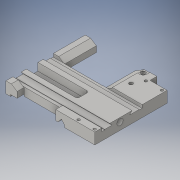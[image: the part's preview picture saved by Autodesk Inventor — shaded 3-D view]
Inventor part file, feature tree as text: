
AUTODESK INVENTOR PART (.ipt)
format: ipt  version: 2016 (Build 200138000, 138)  size: 288,768 bytes
history: native  units: in
note: dims shown in document units (in); Inventor stores cm internally (conversion verified against a paired STEP export)
features: extrude x18, sketch x18
ambient origin geometry x8: Origin, YZ Plane, XZ Plane, XY Plane, X Axis, Y Axis, Z Axis, Center Point
bodies: Solid1 (feature_tree)
feature tree (36):
  extrude  "Extrusion1"  Depth=13.5039in
  extrude  "Extrusion2"  Depth=1.9094in TaperAngle=0.0deg
  extrude  "Extrusion3"  Depth=1.378in
  extrude  "Extrusion4"  Depth=0.8933in
  extrude  "Extrusion5"  Depth=0.0787in
  extrude  "Extrusion6"  Depth=1.1811in
  extrude  "Extrusion7"  Depth=0.1181in
  extrude  "Extrusion8"  Depth=0.3937in
  extrude  "Extrusion10"  Depth=6.5748in
  extrude  "Extrusion11"  Depth=1.9094in TaperAngle=0.0deg
  extrude  "Extrusion12"  Depth=1.9094in TaperAngle=0.0deg
  extrude  "Extrusion16"  Depth=1.2992in TaperAngle=0.0deg
  extrude  "Extrusion17"  Depth=1.2992in
  extrude  "Extrusion18"  Depth=0.9055in
  extrude  "Extrusion19"  Depth=0.3937in
  extrude  "Extrusion20"  Depth=0.0787in TaperAngle=0.0deg
  extrude  "Extrusion21"  Depth=0.0787in TaperAngle=0.0deg
  extrude  "Extrusion22"  Depth=0.0787in TaperAngle=0.0deg
  sketch  "Sketch1"  dims[d0=15.1181in d1=13.5039in]
  sketch  "Sketch3"  dims[d2=1.9094in d3=0.0in d12=1.9094in d13=0.0in]
  sketch  "Sketch7"  dims[d23=1.378in d27=3.7795in]
  sketch  "Sketch8"  dims[d29=1.7323in d32=0.8933in]
  sketch  "Sketch9"  dims[d35=1.9094in d36=0.0in d37=0.0787in]
  sketch  "Sketch10"  dims[d38=0.5118in d43=1.1811in]
  sketch  "Sketch11"  dims[d44=1.9094in d45=0.0in d46=0.1181in]
  sketch  "Sketch12"  dims[d50=0.3937in d52=0.3436in]
  sketch  "Sketch14"  dims[d54=1.9094in d55=0.0in d58=6.5748in]
  sketch  "Sketch17"  dims[d59=5.4724in d60=1.9094in d61=0.0in]
  sketch  "Sketch19"  dims[d65=0.2756in d66=1.9094in d67=0.0in]
  sketch  "Sketch25"  dims[d72=0.3937in d73=1.2992in d74=0.0in]
  sketch  "Sketch26"  dims[d90=1.2992in d91=0.0in d92=1.063in]
  sketch  "Sketch27"  dims[d97=0.6693in d98=0.9055in]
  sketch  "Sketch28"  dims[d101=0.3937in d102=0.0in d109=0.2199in]
  sketch  "Sketch29"  dims[d110=0.3937in d111=0.0in d133=0.0787in d134=0.0in]
  sketch  "Sketch30"  dims[d136=0.748in d137=0.0787in d138=0.0in]
  sketch  "Sketch32"  dims[d139=0.4724in d140=0.0787in d141=0.0in d146=0.4567in d149=0.4567in d152=0.4567in d155=0.4567in d156=0.0in d157=0.0in d159=0.0787in d160=0.0in d161=0.0787in d162=0.0in d168=0.6299in d169=0.3937in d170=0.0in]
